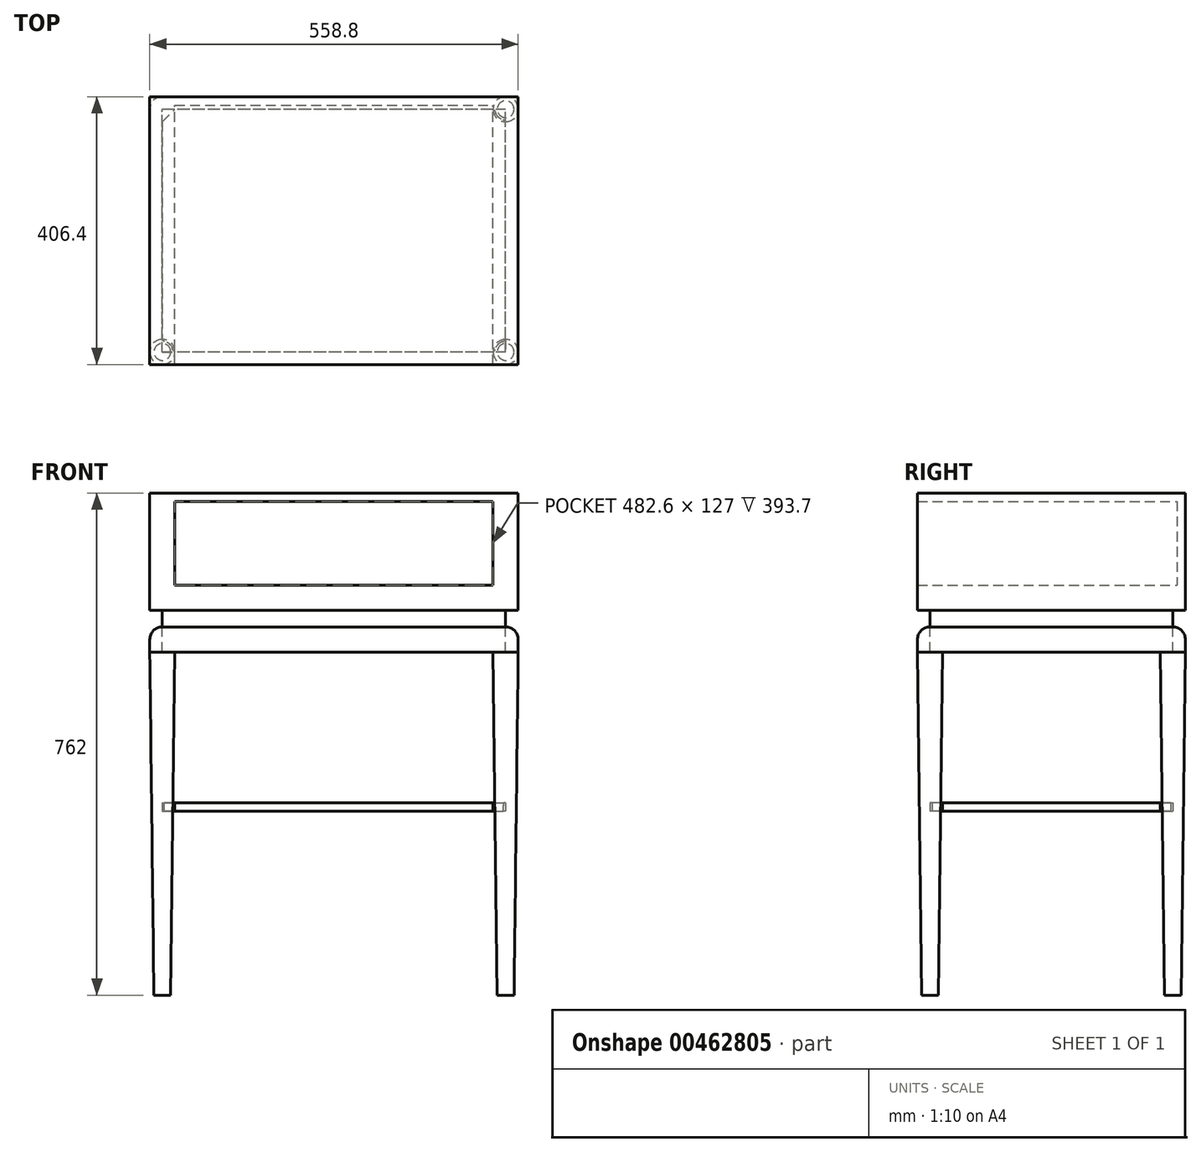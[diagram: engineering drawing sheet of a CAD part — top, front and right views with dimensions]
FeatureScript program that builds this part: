
annotation { "Feature Type Name" : "Feature", "Feature Type Description" : "" }
export const myFeature = defineFeature(function(context is Context, id is Id, definition is map)
    precondition{}
    {
        {
            var Q0;
            Q0=qCreatedBy(makeId("Front.planeOp"),FACE);
            var sketch = newSketch(context, id + "F0", { "sketchPlane" : qUnion([Q0])});
            skLineSegment(sketch, "E0.bottom", {"start": v(-241.3, 0) * mm, "end": v(241.3, 0) * mm});
            skLineSegment(sketch, "E0.top", {"start": v(-241.3, -127) * mm, "end": v(241.3, -127) * mm});
            skLineSegment(sketch, "E0.left", {"start": v(-241.3, 0) * mm, "end": v(-241.3, -127) * mm});
            skLineSegment(sketch, "E0.right", {"start": v(241.3, 0) * mm, "end": v(241.3, -127) * mm});
            skLineSegment(sketch, "E1", {"start": v(-241.3, 0) * mm, "end": v(-279.4, 0) * mm});
            skLineSegment(sketch, "E2", {"start": v(-279.4, 0) * mm, "end": v(-279.4, -165.1) * mm});
            skLineSegment(sketch, "E3", {"start": v(-279.4, -165.1) * mm, "end": v(279.4, -165.1) * mm});
            skLineSegment(sketch, "E4", {"start": v(241.3, 0) * mm, "end": v(279.4, 0) * mm});
            skLineSegment(sketch, "E5", {"start": v(279.4, 0) * mm, "end": v(279.4, -165.1) * mm});
            skLineSegment(sketch, "E6", {"start": v(-171.76, -127) * mm, "end": v(-171.76, -165.1) * mm, "construction": true});
            skLineSegment(sketch, "E7", {"start": v(-279.4, 0) * mm, "end": v(-279.4, 12.7) * mm});
            skLineSegment(sketch, "E8", {"start": v(-279.4, 12.7) * mm, "end": v(279.4, 12.7) * mm});
            skLineSegment(sketch, "E9", {"start": v(279.4, 12.7) * mm, "end": v(279.4, 0) * mm});
            skSolve(sketch);
        }
        {
            var Q0;
            Q0 = qSketchRegion(id + "F0", true);
            extrude(context, id + "F1", {"entities" : qUnion([Q0]), "endBound" : BoundingType.SYMMETRIC, "depth" : 406.4 * mm, "offsetDistance" : 25.4 * mm});
        }
        {
            var Q0;
            Q0=makeQuery(id+"F1.opExtrude","SWEPT_FACE",FACE,{"disambiguationData":[OSD([sQuery(id+"F0.wireOp",EDGE,"E3")])]});
            var sketch = newSketch(context, id + "F2", { "sketchPlane" : qUnion([Q0])});
            skLineSegment(sketch, "E10.0", {"start": v(-279.4, 203.2) * mm, "end": v(279.4, 203.2) * mm, "construction": true});
            skLineSegment(sketch, "E11.0", {"start": v(-279.4, 203.2) * mm, "end": v(-279.4, -203.2) * mm, "construction": true});
            skLineSegment(sketch, "E12.0", {"start": v(-279.4, -203.2) * mm, "end": v(279.4, -203.2) * mm, "construction": true});
            skLineSegment(sketch, "E13.0", {"start": v(279.4, 203.2) * mm, "end": v(279.4, -203.2) * mm, "construction": true});
            skLineSegment(sketch, "E14.bottom", {"start": v(260.35, -184.15) * mm, "end": v(-260.35, -184.15) * mm});
            skLineSegment(sketch, "E14.top", {"start": v(260.35, 184.15) * mm, "end": v(-260.35, 184.15) * mm});
            skLineSegment(sketch, "E14.left", {"start": v(260.35, -184.15) * mm, "end": v(260.35, 184.15) * mm});
            skLineSegment(sketch, "E14.right", {"start": v(-260.35, -184.15) * mm, "end": v(-260.35, 184.15) * mm});
            skPoint(sketch, "E14.middle", {"position": v(0, 0) * mm});
            skLineSegment(sketch, "E15", {"start": v(-260.35, 203.2) * mm, "end": v(-260.35, 184.15) * mm, "construction": true});
            skLineSegment(sketch, "E16", {"start": v(-260.35, -184.15) * mm, "end": v(-260.35, -203.2) * mm, "construction": true});
            skLineSegment(sketch, "E17", {"start": v(-260.35, -184.15) * mm, "end": v(-279.4, -184.15) * mm, "construction": true});
            skLineSegment(sketch, "E18", {"start": v(260.35, -184.15) * mm, "end": v(279.4, -184.15) * mm, "construction": true});
            skSolve(sketch);
        }
        {
            var Q0;
            Q0 = qSketchRegion(id + "F2", true);
            extrude(context, id + "F3", {"entities" : qUnion([Q0]), "operationType" : NewBodyOperationType.ADD, "depth" : 25.4 * mm, "offsetDistance" : 25.4 * mm});
        }
        {
            var Q0;
            Q0=makeQuery(id+"F3.opExtrude","CAP_FACE",FACE,{"disambiguationData":[OSD([sQuery(id+"F2.wireOp",EDGE,"E14.bottom"),sQuery(id+"F2.wireOp",EDGE,"E14.top"),sQuery(id+"F2.wireOp",EDGE,"E14.left"),sQuery(id+"F2.wireOp",EDGE,"E14.right")])],"isStart":false});
            var sketch = newSketch(context, id + "F4", { "sketchPlane" : qUnion([Q0])});
            skLineSegment(sketch, "E19.0", {"start": v(-279.4, 203.2) * mm, "end": v(-279.4, -203.2) * mm, "construction": true});
            skLineSegment(sketch, "E20.0", {"start": v(-279.4, 203.2) * mm, "end": v(279.4, 203.2) * mm, "construction": true});
            skLineSegment(sketch, "E21.0", {"start": v(279.4, 203.2) * mm, "end": v(279.4, -203.2) * mm, "construction": true});
            skLineSegment(sketch, "E22.0", {"start": v(-279.4, -203.2) * mm, "end": v(279.4, -203.2) * mm, "construction": true});
            skLineSegment(sketch, "E23.0.0", {"start": v(-279.4, -203.2) * mm, "end": v(279.4, -203.2) * mm});
            skLineSegment(sketch, "E23.0.1", {"start": v(279.4, -203.2) * mm, "end": v(279.4, 203.2) * mm});
            skLineSegment(sketch, "E23.0.2", {"start": v(279.4, 203.2) * mm, "end": v(-279.4, 203.2) * mm});
            skLineSegment(sketch, "E23.0.3", {"start": v(-279.4, 203.2) * mm, "end": v(-279.4, -203.2) * mm});
            skSolve(sketch);
        }
        {
            var Q0;
            Q0=makeQuery(id+"F4.imprint","IMPRINT",FACE,{"disambiguationData":[TD([[makeQuery(id+"F4.imprint","IMPRINT",EDGE,{"derivedFrom":sQuery(id+"F4.wireOp",EDGE,"E23.0.0")}),1.0]])]});
            extrude(context, id + "F5", {"entities" : qUnion([Q0]), "depth" : 38.1 * mm});
        }
        {
            var Q0;
            Q0=makeQuery(id+"F5.opExtrude","CAP_EDGE",EDGE,{"disambiguationData":[OSD([sQuery(id+"F4.wireOp",EDGE,"E23.0.3")])],"isStart":true});
            var Q1;
            Q1=makeQuery(id+"F5.opExtrude","CAP_EDGE",EDGE,{"disambiguationData":[OSD([sQuery(id+"F4.wireOp",EDGE,"E23.0.2")])],"isStart":true});
            var Q2;
            Q2=makeQuery(id+"F5.opExtrude","SWEPT_EDGE",EDGE,{"disambiguationData":[OSD([sQuery(id+"F4.wireOp",EDGE,"E23.0.2"),sQuery(id+"F4.wireOp",EDGE,"E23.0.3")])]});
            var Q3;
            Q3=makeQuery(id+"F5.opExtrude","SWEPT_EDGE",EDGE,{"disambiguationData":[OSD([sQuery(id+"F4.wireOp",EDGE,"E23.0.1"),sQuery(id+"F4.wireOp",EDGE,"E23.0.2")])]});
            var Q4;
            Q4=makeQuery(id+"F5.opExtrude","CAP_EDGE",EDGE,{"disambiguationData":[OSD([sQuery(id+"F4.wireOp",EDGE,"E23.0.1")])],"isStart":true});
            var Q5;
            Q5=makeQuery(id+"F5.opExtrude","SWEPT_EDGE",EDGE,{"disambiguationData":[OSD([sQuery(id+"F4.wireOp",EDGE,"E23.0.0"),sQuery(id+"F4.wireOp",EDGE,"E23.0.1")])]});
            var Q6;
            Q6=makeQuery(id+"F5.opExtrude","CAP_EDGE",EDGE,{"disambiguationData":[OSD([sQuery(id+"F4.wireOp",EDGE,"E23.0.0")])],"isStart":true});
            var Q7;
            Q7=makeQuery(id+"F5.opExtrude","SWEPT_EDGE",EDGE,{"disambiguationData":[OSD([sQuery(id+"F4.wireOp",EDGE,"E23.0.0"),sQuery(id+"F4.wireOp",EDGE,"E23.0.3")])]});
            fillet(context, id + "F6", {"entities" : qUnion([Q0, Q1, Q2, Q3, Q4, Q5, Q6, Q7]), "radius" : 19.05 * mm, "tangentPropagation" : true, "allowEdgeOverflow" : false});
        }
        {
            var Q0;
            Q0=makeQuery(id+"F5.opExtrude","CAP_FACE",FACE,{"disambiguationData":[OSD([sQuery(id+"F2.wireOp",EDGE,"E14.bottom"),sQuery(id+"F2.wireOp",EDGE,"E14.top"),sQuery(id+"F2.wireOp",EDGE,"E14.left"),sQuery(id+"F2.wireOp",EDGE,"E14.right"),sQuery(id+"F4.wireOp",EDGE,"E23.0.0"),sQuery(id+"F4.wireOp",EDGE,"E23.0.1"),sQuery(id+"F4.wireOp",EDGE,"E23.0.2"),sQuery(id+"F4.wireOp",EDGE,"E23.0.3")])],"isStart":false});
            var sketch = newSketch(context, id + "F7", { "sketchPlane" : qUnion([Q0])});
            skArc(sketch, "E24.0", {"start": v(-260.35, 203.2) * mm, "mid": v(-273.82, 197.62) * mm, "end": v(-279.4, 184.15) * mm});
            skArc(sketch, "E25.0", {"start": v(-279.4, -184.15) * mm, "mid": v(-273.82, -197.62) * mm, "end": v(-260.35, -203.2) * mm});
            skArc(sketch, "E26.0", {"start": v(260.35, -203.2) * mm, "mid": v(273.82, -197.62) * mm, "end": v(279.4, -184.15) * mm});
            skArc(sketch, "E27.0", {"start": v(279.4, 184.15) * mm, "mid": v(273.82, 197.62) * mm, "end": v(260.35, 203.2) * mm});
            skArc(sketch, "E28", {"start": v(-279.4, 184.15) * mm, "mid": v(-246.88, 170.68) * mm, "end": v(-260.35, 203.2) * mm});
            skLineSegment(sketch, "E29", {"start": v(-279.4, 0) * mm, "end": v(279.4, 0) * mm, "construction": true});
            skLineSegment(sketch, "E30", {"start": v(0, -203.2) * mm, "end": v(0, 203.2) * mm, "construction": true});
            skArc(sketch, "E31.MirrorCS", {"start": v(279.4, 184.15) * mm, "mid": v(246.88, 170.68) * mm, "end": v(260.35, 203.2) * mm});
            skArc(sketch, "E32.MirrorCS", {"start": v(260.35, 203.2) * mm, "mid": v(273.82, 197.62) * mm, "end": v(279.4, 184.15) * mm});
            skLineSegment(sketch, "E33.MirrorCS", {"start": v(279.4, 0) * mm, "end": v(-279.4, 0) * mm, "construction": true});
            skArc(sketch, "E34.MirrorCS", {"start": v(-279.4, -184.15) * mm, "mid": v(-246.88, -170.68) * mm, "end": v(-260.35, -203.2) * mm});
            skArc(sketch, "E35.MirrorCS", {"start": v(279.4, -184.15) * mm, "mid": v(246.88, -170.68) * mm, "end": v(260.35, -203.2) * mm});
            skSolve(sketch);
        }
        {
            var Q0;
            Q0=makeQuery(id+"F1.opExtrude","SWEPT_FACE",FACE,{"disambiguationData":[OSD([sQuery(id+"F0.wireOp",EDGE,"E8")])]});
            cPlane(context, id + "F8", {"entities" : qUnion([Q0]), "cplaneType" : CPlaneType.OFFSET, "offset" : 762 * mm, "oppositeDirection" : true, "width" : 152.4 * mm, "height" : 152.4 * mm});
        }
        {
            var Q0;
            Q0=qCreatedBy(id+"F8.planeOp",FACE);
            var sketch = newSketch(context, id + "F9", { "sketchPlane" : qUnion([Q0])});
            skPoint(sketch, "E36.0", {"position": v(-260.35, -184.15) * mm});
            skPoint(sketch, "E37.0", {"position": v(260.35, -184.15) * mm});
            skPoint(sketch, "E38.0", {"position": v(260.35, 184.15) * mm});
            skPoint(sketch, "E39.0", {"position": v(-260.35, 184.15) * mm});
            skCircle(sketch, "E40", {"center": v(-260.35, -184.15) * mm, "radius": 12.7 * mm});
            skCircle(sketch, "E41.MirrorC", {"center": v(-260.35, 184.15) * mm, "radius": 12.7 * mm});
            skCircle(sketch, "E42.MirrorC", {"center": v(260.35, -184.15) * mm, "radius": 12.7 * mm});
            skCircle(sketch, "E43.MirrorC", {"center": v(260.35, 184.15) * mm, "radius": 12.7 * mm});
            skSolve(sketch);
        }
        {
            var Q0;
            Q0=sQuery(id+"F7.wireOp",VERTEX,"E31.MirrorCS.center");
            var Q1;
            Q1=sQuery(id+"F7.wireOp",VERTEX,"E26.0.center");
            var Q2;
            Q2=sQuery(id+"F9.wireOp",VERTEX,"E38.0");
            cPlane(context, id + "F10", {"entities" : qUnion([Q0, Q1, Q2]), "cplaneType" : CPlaneType.THREE_POINT, "offset" : 25.4 * mm, "width" : 152.4 * mm, "height" : 152.4 * mm});
        }
        {
            var Q0;
            Q0=qCreatedBy(id+"F10.planeOp",FACE);
            var sketch = newSketch(context, id + "F11", { "sketchPlane" : qUnion([Q0])});
            skLineSegment(sketch, "E44.0", {"start": v(203.2, -228.6) * mm, "end": v(-203.2, -228.6) * mm, "construction": true});
            skPoint(sketch, "E45.0", {"position": v(-184.15, -749.3) * mm});
            skLineSegment(sketch, "E46", {"start": v(-203.2, -228.6) * mm, "end": v(-184.15, -228.6) * mm});
            skLineSegment(sketch, "E47", {"start": v(-184.15, -228.6) * mm, "end": v(-184.15, -749.3) * mm});
            skLineSegment(sketch, "E48", {"start": v(-196.92, -749.3) * mm, "end": v(-203.2, -228.6) * mm});
            skLineSegment(sketch, "E49", {"start": v(-196.92, -749.3) * mm, "end": v(-184.15, -749.3) * mm});
            skSolve(sketch);
        }
        {
            var Q0;
            Q0 = qSketchRegion(id + "F11", true);
            var Q1;
            Q1=sQuery(id+"F11.wireOp",EDGE,"E47");
            revolve(context, id + "F12", {"operationType" : NewBodyOperationType.ADD, "entities" : qUnion([Q0]), "axis" : qUnion([Q1]), "revolveType" : RevolveType.FULL});
        }
        {
            var Q0;
            Q0=makeQuery(id+"F5.opExtrude","SWEPT_BODY",BODY,{"disambiguationData":[OSD([sQuery(id+"F2.wireOp",EDGE,"E14.bottom"),sQuery(id+"F2.wireOp",EDGE,"E14.top"),sQuery(id+"F2.wireOp",EDGE,"E14.left"),sQuery(id+"F2.wireOp",EDGE,"E14.right"),sQuery(id+"F4.wireOp",EDGE,"E23.0.0"),sQuery(id+"F4.wireOp",EDGE,"E23.0.1"),sQuery(id+"F4.wireOp",EDGE,"E23.0.2"),sQuery(id+"F4.wireOp",EDGE,"E23.0.3")])]});
            var Q1;
            Q1=qCreatedBy(makeId("Front.planeOp"),FACE);
            mirror(context, id + "F13", {"operationType" : NewBodyOperationType.ADD, "entities" : qUnion([Q0]), "mirrorPlane" : qUnion([Q1])});
        }
        {
            var Q0;
            Q0=makeQuery(id+"F5.opExtrude","SWEPT_BODY",BODY,{"disambiguationData":[OSD([sQuery(id+"F2.wireOp",EDGE,"E14.bottom"),sQuery(id+"F2.wireOp",EDGE,"E14.top"),sQuery(id+"F2.wireOp",EDGE,"E14.left"),sQuery(id+"F2.wireOp",EDGE,"E14.right"),sQuery(id+"F4.wireOp",EDGE,"E23.0.0"),sQuery(id+"F4.wireOp",EDGE,"E23.0.1"),sQuery(id+"F4.wireOp",EDGE,"E23.0.2"),sQuery(id+"F4.wireOp",EDGE,"E23.0.3")])]});
            var Q1;
            Q1=qCreatedBy(makeId("Right.planeOp"),FACE);
            mirror(context, id + "F14", {"operationType" : NewBodyOperationType.ADD, "entities" : qUnion([Q0]), "mirrorPlane" : qUnion([Q1])});
        }
        {
            var Q0;
            Q0=makeQuery(id+"F1.opExtrude","CAP_FACE",FACE,{"disambiguationData":[OSD([sQuery(id+"F0.wireOp",EDGE,"E0.bottom"),sQuery(id+"F0.wireOp",EDGE,"E0.top"),sQuery(id+"F0.wireOp",EDGE,"E0.left"),sQuery(id+"F0.wireOp",EDGE,"E0.right"),sQuery(id+"F0.wireOp",EDGE,"E2"),sQuery(id+"F0.wireOp",EDGE,"E3"),sQuery(id+"F0.wireOp",EDGE,"E5"),sQuery(id+"F0.wireOp",EDGE,"E7"),sQuery(id+"F0.wireOp",EDGE,"E8"),sQuery(id+"F0.wireOp",EDGE,"E9")])],"isStart":true});
            var sketch = newSketch(context, id + "F15", { "sketchPlane" : qUnion([Q0])});
            skLineSegment(sketch, "E50.0", {"start": v(241.3, 0) * mm, "end": v(-241.3, 0) * mm});
            skLineSegment(sketch, "E51.0", {"start": v(-241.3, 0) * mm, "end": v(-241.3, -127) * mm});
            skLineSegment(sketch, "E52.0", {"start": v(241.3, -127) * mm, "end": v(-241.3, -127) * mm});
            skLineSegment(sketch, "E53.0", {"start": v(241.3, 0) * mm, "end": v(241.3, -127) * mm});
            skSolve(sketch);
        }
        {
            var Q0;
            Q0=makeQuery(id+"F15.imprint","IMPRINT",FACE,{"disambiguationData":[TD([[makeQuery(id+"F15.imprint","IMPRINT",EDGE,{"derivedFrom":sQuery(id+"F15.wireOp",EDGE,"E50.0")}),1.0]])]});
            extrude(context, id + "F16", {"entities" : qUnion([Q0]), "operationType" : NewBodyOperationType.ADD, "oppositeDirection" : true, "depth" : 12.7 * mm});
        }
        {
            var Q0;
            Q0=qCreatedBy(id+"F8.planeOp",FACE);
            cPlane(context, id + "F17", {"entities" : qUnion([Q0]), "cplaneType" : CPlaneType.OFFSET, "offset" : 279.4 * mm, "width" : 152.4 * mm, "height" : 152.4 * mm});
        }
        {
            var Q0;
            Q0=qCreatedBy(id+"F17.planeOp",FACE);
            var sketch = newSketch(context, id + "F18", { "sketchPlane" : qUnion([Q0])});
            skLineSegment(sketch, "E54.0", {"start": v(241.3, -184.15) * mm, "end": v(-241.3, -184.15) * mm});
            skLineSegment(sketch, "E55.0", {"start": v(-260.35, 165.1) * mm, "end": v(-260.35, -165.1) * mm});
            skLineSegment(sketch, "E56.0", {"start": v(241.3, 184.15) * mm, "end": v(-241.3, 184.15) * mm});
            skLineSegment(sketch, "E57.0", {"start": v(260.35, 165.1) * mm, "end": v(260.35, -165.1) * mm});
            skLineSegment(sketch, "E58", {"start": v(-260.35, -165.1) * mm, "end": v(-241.3, -184.15) * mm});
            skLineSegment(sketch, "E59.MirrorCS", {"start": v(-260.35, 165.1) * mm, "end": v(-241.3, 184.15) * mm});
            skLineSegment(sketch, "E60.MirrorCS", {"start": v(260.35, -165.1) * mm, "end": v(241.3, -184.15) * mm});
            skLineSegment(sketch, "E61.MirrorCS", {"start": v(260.35, 165.1) * mm, "end": v(241.3, 184.15) * mm});
            skSolve(sketch);
        }
        {
            var Q0;
            Q0 = qSketchRegion(id + "F18", true);
            extrude(context, id + "F19", {"entities" : qUnion([Q0]), "operationType" : NewBodyOperationType.ADD, "depth" : 12.7 * mm});
        }
    });
